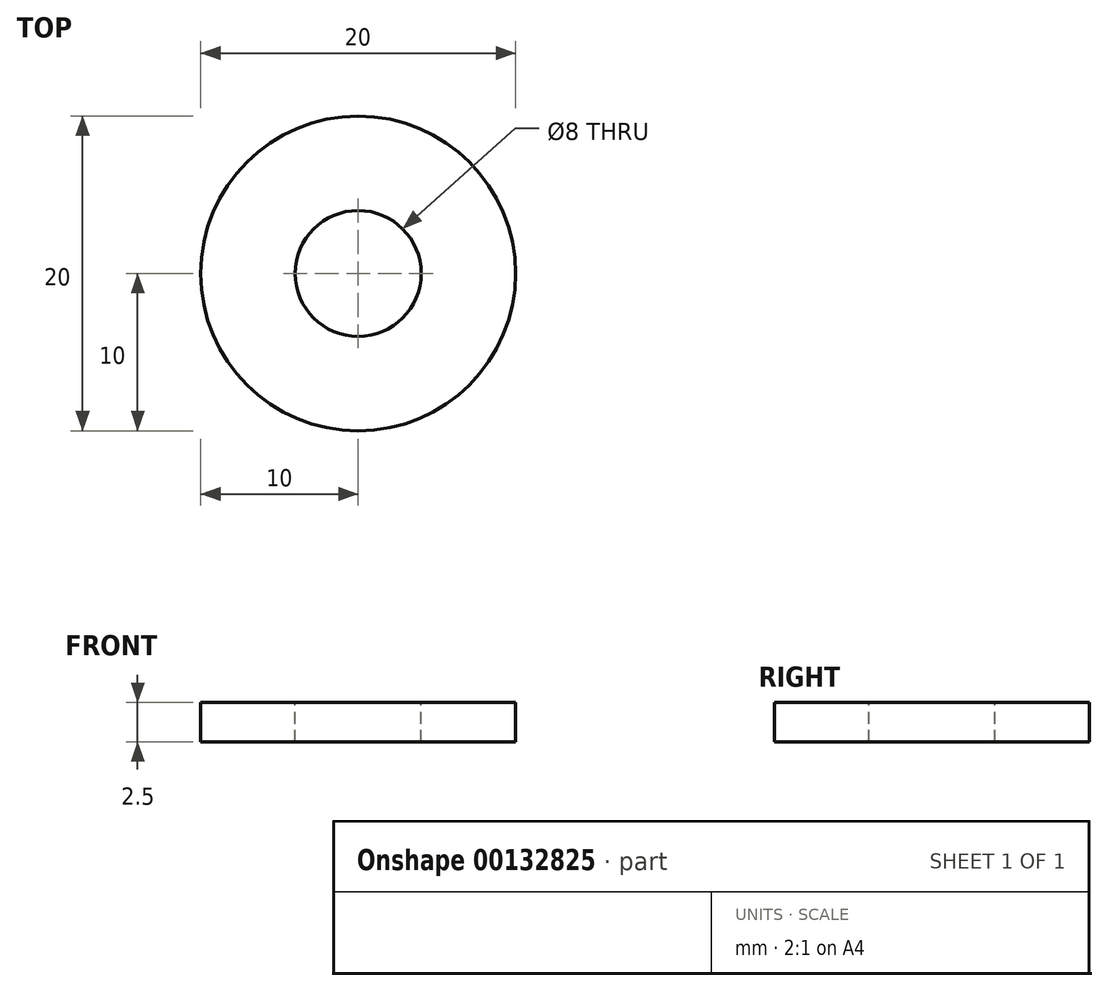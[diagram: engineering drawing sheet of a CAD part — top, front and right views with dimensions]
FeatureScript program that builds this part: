
annotation { "Feature Type Name" : "Feature", "Feature Type Description" : "" }
export const myFeature = defineFeature(function(context is Context, id is Id, definition is map)
    precondition{}
    {
        {
            assignVariable(context, id + "F0", {"name" : "L", "anyValue" : 2.5});
        }
        {
            var Q0;
            Q0=qCreatedBy(makeId("Top.planeOp"),FACE);
            var sketch = newSketch(context, id + "F1", { "sketchPlane" : qUnion([Q0])});
            skCircle(sketch, "E0", {"center": v(0, 0) * mm, "radius": 10 * mm});
            skCircle(sketch, "E1", {"center": v(0, 0) * mm, "radius": 4 * mm});
            skCircle(sketch, "E2", {"center": v(0, 0) * mm, "radius": 2.5 * mm});
            skSolve(sketch);
        }
        {
            var Q0;
            Q0=makeQuery(id+"F1.imprint","IMPRINT",FACE,{"disambiguationData":[TD([[makeQuery(id+"F1.imprint","IMPRINT",EDGE,{"derivedFrom":sQuery(id+"F1.wireOp",EDGE,"E0")}),1.0]])]});
            var Q1;
            Q1=makeQuery(id+"F1.imprint","IMPRINT",FACE,{"disambiguationData":[TD([[makeQuery(id+"F1.imprint","IMPRINT",EDGE,{"derivedFrom":sQuery(id+"F1.wireOp",EDGE,"E1")}),1.0]])]});
            var Q2;
            Q2=makeQuery(id+"F1.imprint","IMPRINT",FACE,{"disambiguationData":[TD([[makeQuery(id+"F1.imprint","IMPRINT",EDGE,{"derivedFrom":sQuery(id+"F1.wireOp",EDGE,"E2")}),1.0]])]});
            extrude(context, id + "F2", {"entities" : qUnion([Q0, Q1, Q2]), "endBound" : BoundingType.SYMMETRIC, "depth" : (getVariable(context, 'L')) * mm});
        }
        {
            var Q0;
            Q0=makeQuery(id+"F2.opExtrude","CAP_FACE",FACE,{"disambiguationData":[OSD([sQuery(id+"F1.wireOp",EDGE,"E0")])],"isStart":false});
            var sketch = newSketch(context, id + "F3", { "sketchPlane" : qUnion([Q0])});
            skCircle(sketch, "E3.0", {"center": v(0, 0) * mm, "radius": 4 * mm});
            skSolve(sketch);
        }
        {
            var Q0;
            Q0=makeQuery(id+"F3.imprint","IMPRINT",FACE,{"disambiguationData":[TD([[makeQuery(id+"F3.imprint","IMPRINT",EDGE,{"derivedFrom":sQuery(id+"F3.wireOp",EDGE,"E3.0")}),1.0]])]});
            extrude(context, id + "F4", {"entities" : qUnion([Q0]), "operationType" : NewBodyOperationType.REMOVE, "oppositeDirection" : true, "depth" : 10 * mm});
        }
        {
            var Q0;
            Q0=makeQuery(id+"F2.opExtrude","CAP_FACE",FACE,{"disambiguationData":[OSD([sQuery(id+"F1.wireOp",EDGE,"E0")])],"isStart":true});
            var sketch = newSketch(context, id + "F5", { "sketchPlane" : qUnion([Q0])});
            skCircle(sketch, "E4.0", {"center": v(0, 0) * mm, "radius": 2.5 * mm});
            skSolve(sketch);
        }
        {
            var Q0;
            Q0=makeQuery(id+"F5.imprint","IMPRINT",FACE,{"disambiguationData":[TD([[makeQuery(id+"F5.imprint","IMPRINT",EDGE,{"derivedFrom":sQuery(id+"F5.wireOp",EDGE,"E4.0")}),-1.0]])]});
            extrude(context, id + "F6", {"entities" : qUnion([Q0]), "operationType" : NewBodyOperationType.REMOVE, "oppositeDirection" : true, "depth" : 10 * mm});
        }
    });
